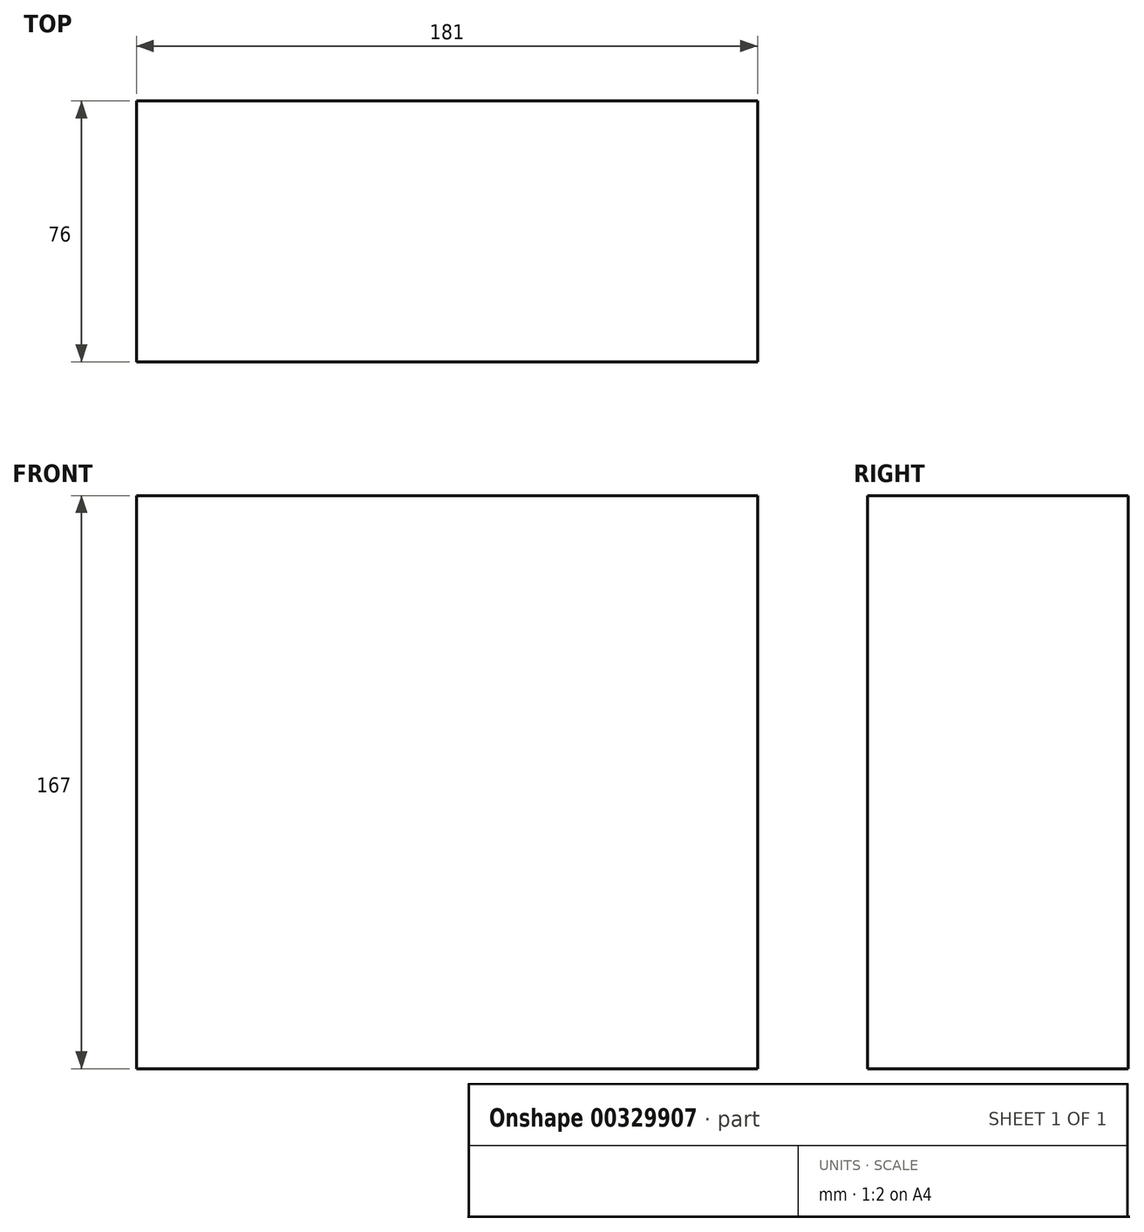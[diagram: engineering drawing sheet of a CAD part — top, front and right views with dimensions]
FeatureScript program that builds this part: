
annotation { "Feature Type Name" : "Feature", "Feature Type Description" : "" }
export const myFeature = defineFeature(function(context is Context, id is Id, definition is map)
    precondition{}
    {
        {
            var Q0;
            Q0=qCreatedBy(makeId("Top.planeOp"),FACE);
            var sketch = newSketch(context, id + "F0", { "sketchPlane" : qUnion([Q0])});
            skLineSegment(sketch, "E0.bottom", {"start": v(90.5, 38) * mm, "end": v(-90.5, 38) * mm});
            skLineSegment(sketch, "E0.top", {"start": v(90.5, -38) * mm, "end": v(-90.5, -38) * mm});
            skLineSegment(sketch, "E0.left", {"start": v(90.5, 38) * mm, "end": v(90.5, -38) * mm});
            skLineSegment(sketch, "E0.right", {"start": v(-90.5, 38) * mm, "end": v(-90.5, -38) * mm});
            skPoint(sketch, "E0.middle", {"position": v(0, 0) * mm});
            skSolve(sketch);
        }
        {
            var Q0;
            Q0=makeQuery(id+"F0.imprint","IMPRINT",FACE,{"disambiguationData":[TD([[makeQuery(id+"F0.imprint","IMPRINT",EDGE,{"derivedFrom":sQuery(id+"F0.wireOp",EDGE,"E0.bottom")}),1.0]])]});
            extrude(context, id + "F1", {"entities" : qUnion([Q0]), "depth" : 167 * mm, "symmetric" : true});
        }
    });
